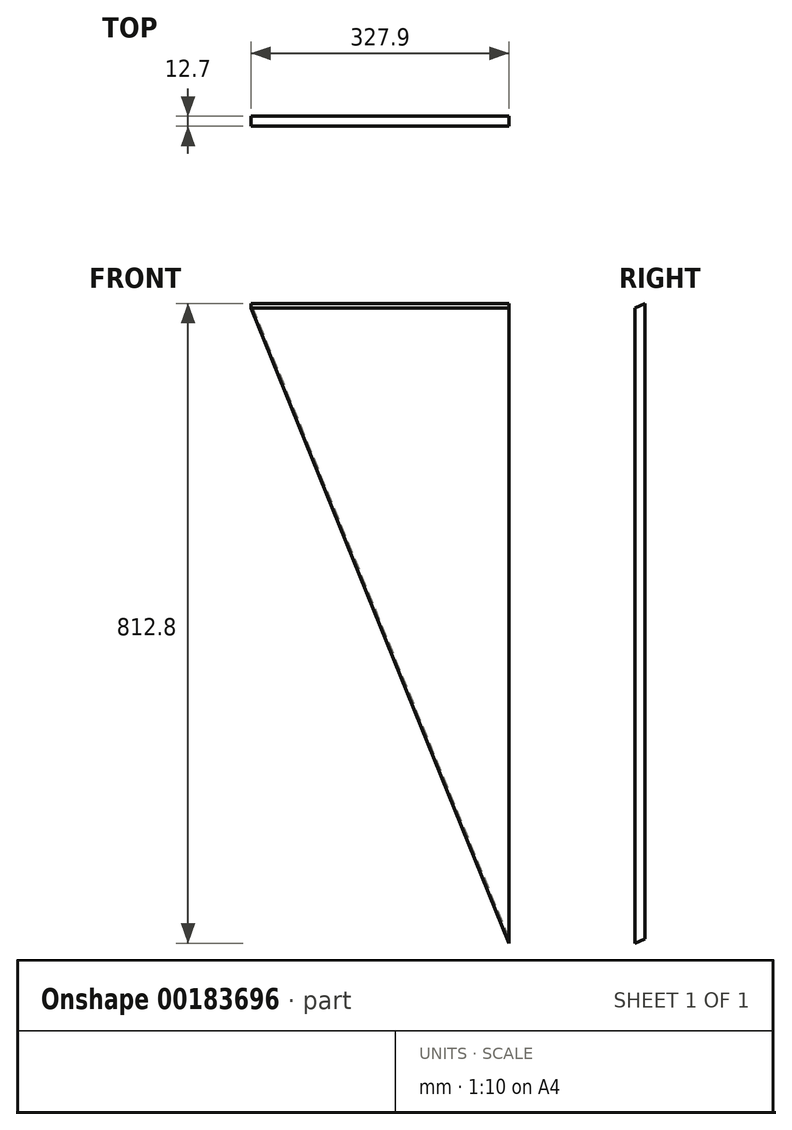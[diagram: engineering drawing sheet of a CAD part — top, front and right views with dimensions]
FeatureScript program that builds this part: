
annotation { "Feature Type Name" : "Feature", "Feature Type Description" : "" }
export const myFeature = defineFeature(function(context is Context, id is Id, definition is map)
    precondition{}
    {
        {
            var Q0;
            Q0=qCreatedBy(makeId("Front.planeOp"),FACE);
            var sketch = newSketch(context, id + "F0", { "sketchPlane" : qUnion([Q0])});
            skLineSegment(sketch, "E0", {"start": v(-123.42, 184.34) * mm, "end": v(206.78, 184.34) * mm});
            skLineSegment(sketch, "E1", {"start": v(206.78, 184.34) * mm, "end": v(206.78, -628.46) * mm});
            skLineSegment(sketch, "E2", {"start": v(206.78, -628.46) * mm, "end": v(-123.42, 184.34) * mm});
            skSolve(sketch);
        }
        {
            var Q0;
            Q0=qSketchRegion(id+"F0",true);
            extrude(context, id + "F1", {"entities" : qUnion([Q0]), "endBound" : BoundingType.SYMMETRIC, "depth" : 12.7 * mm});
        }
        {
            var Q0;
            Q0=makeQuery(id+"F1.opExtrude","SWEPT_EDGE",EDGE,{"disambiguationData":[OSD([sQuery(id+"F0.wireOp",EDGE,"E0"),sQuery(id+"F0.wireOp",EDGE,"E2")])]});
            var Q1;
            Q1=makeQuery(id+"F1.opExtrude","CAP_EDGE",EDGE,{"disambiguationData":[OSD([sQuery(id+"F0.wireOp",EDGE,"E2")])],"isStart":true});
            cPlane(context, id + "F2", {"entities" : qUnion([Q0, Q1]), "cplaneType" : CPlaneType.LINE_ANGLE, "offset" : 25.4 * mm, "angle" : 90 * degree, "width" : 152.4 * mm, "height" : 152.4 * mm});
        }
        {
            var Q0;
            Q0=makeQuery(id+"F1.opExtrude","SWEPT_FACE",FACE,{"disambiguationData":[OSD([sQuery(id+"F0.wireOp",EDGE,"E1")])]});
            var sketch = newSketch(context, id + "F3", { "sketchPlane" : qUnion([Q0])});
            skLineSegment(sketch, "E3", {"start": v(6.35, 184.34) * mm, "end": v(-6.35, 178.69) * mm});
            skLineSegment(sketch, "E4", {"start": v(6.35, 184.34) * mm, "end": v(-6.35, 184.34) * mm});
            skLineSegment(sketch, "E5", {"start": v(-6.35, 184.34) * mm, "end": v(-6.35, 178.69) * mm});
            skSolve(sketch);
        }
        {
            var Q0;
            Q0=qSketchRegion(id+"F3",true);
            extrude(context, id + "F4", {"entities" : qUnion([Q0]), "operationType" : NewBodyOperationType.REMOVE, "endBound" : BoundingType.THROUGH_ALL, "oppositeDirection" : true, "depth" : 25.4 * mm});
        }
        {
            var Q0;
            Q0=qCreatedBy(id+"F2.planeOp",FACE);
            var sketch = newSketch(context, id + "F5", { "sketchPlane" : qUnion([Q0])});
            skLineSegment(sketch, "E6", {"start": v(-44.96, -6.48) * mm, "end": v(-44.96, 6.35) * mm});
            skLineSegment(sketch, "E7", {"start": v(-44.96, 6.35) * mm, "end": v(-42.81, -6.48) * mm});
            skLineSegment(sketch, "E8", {"start": v(-42.81, -6.48) * mm, "end": v(-44.96, -6.48) * mm});
            skSolve(sketch);
        }
        {
            var Q0;
            Q0 = qSketchRegion(id + "F5", true);
            extrude(context, id + "F6", {"entities" : qUnion([Q0]), "operationType" : NewBodyOperationType.REMOVE, "endBound" : BoundingType.THROUGH_ALL, "depth" : 25.4 * mm});
        }
    });
